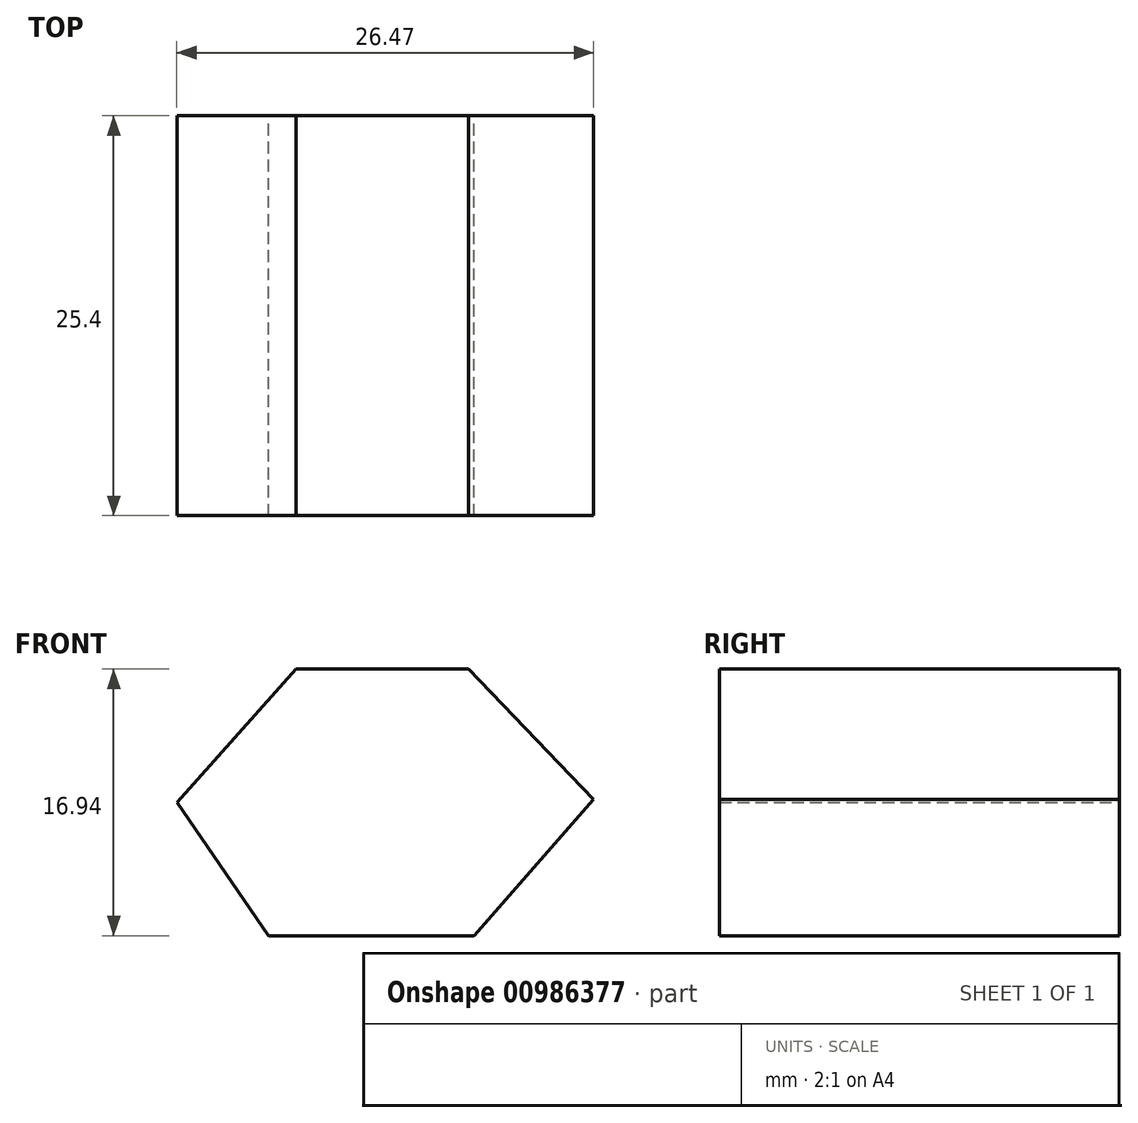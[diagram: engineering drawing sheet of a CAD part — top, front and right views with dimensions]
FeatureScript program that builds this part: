
annotation { "Feature Type Name" : "Feature", "Feature Type Description" : "" }
export const myFeature = defineFeature(function(context is Context, id is Id, definition is map)
    precondition{}
    {
        {
            var Q0;
            Q0=qCreatedBy(makeId("Front.planeOp"),FACE);
            var sketch = newSketch(context, id + "F0", { "sketchPlane" : qUnion([Q0])});
            skLineSegment(sketch, "E0", {"start": v(-14.48, 5.5) * mm, "end": v(-6.89, 13.96) * mm});
            skLineSegment(sketch, "E1", {"start": v(-6.89, 13.96) * mm, "end": v(4.05, 13.96) * mm});
            skLineSegment(sketch, "E2", {"start": v(4.05, 13.96) * mm, "end": v(12, 5.67) * mm});
            skLineSegment(sketch, "E3", {"start": v(12, 5.67) * mm, "end": v(4.4, -2.98) * mm});
            skLineSegment(sketch, "E4", {"start": v(4.4, -2.98) * mm, "end": v(-8.65, -2.98) * mm});
            skLineSegment(sketch, "E5", {"start": v(-8.65, -2.98) * mm, "end": v(-14.48, 5.5) * mm});
            skSolve(sketch);
        }
        {
            var Q0;
            Q0=makeQuery(id+"F0.imprint","IMPRINT",FACE,{"disambiguationData":[TD([[makeQuery(id+"F0.imprint","IMPRINT",EDGE,{"derivedFrom":sQuery(id+"F0.wireOp",EDGE,"E0")}),-1.0]])]});
            extrude(context, id + "F1", {"entities" : qUnion([Q0]), "depth" : 25.4 * mm, "offsetDistance" : 25.4 * mm});
        }
    });
